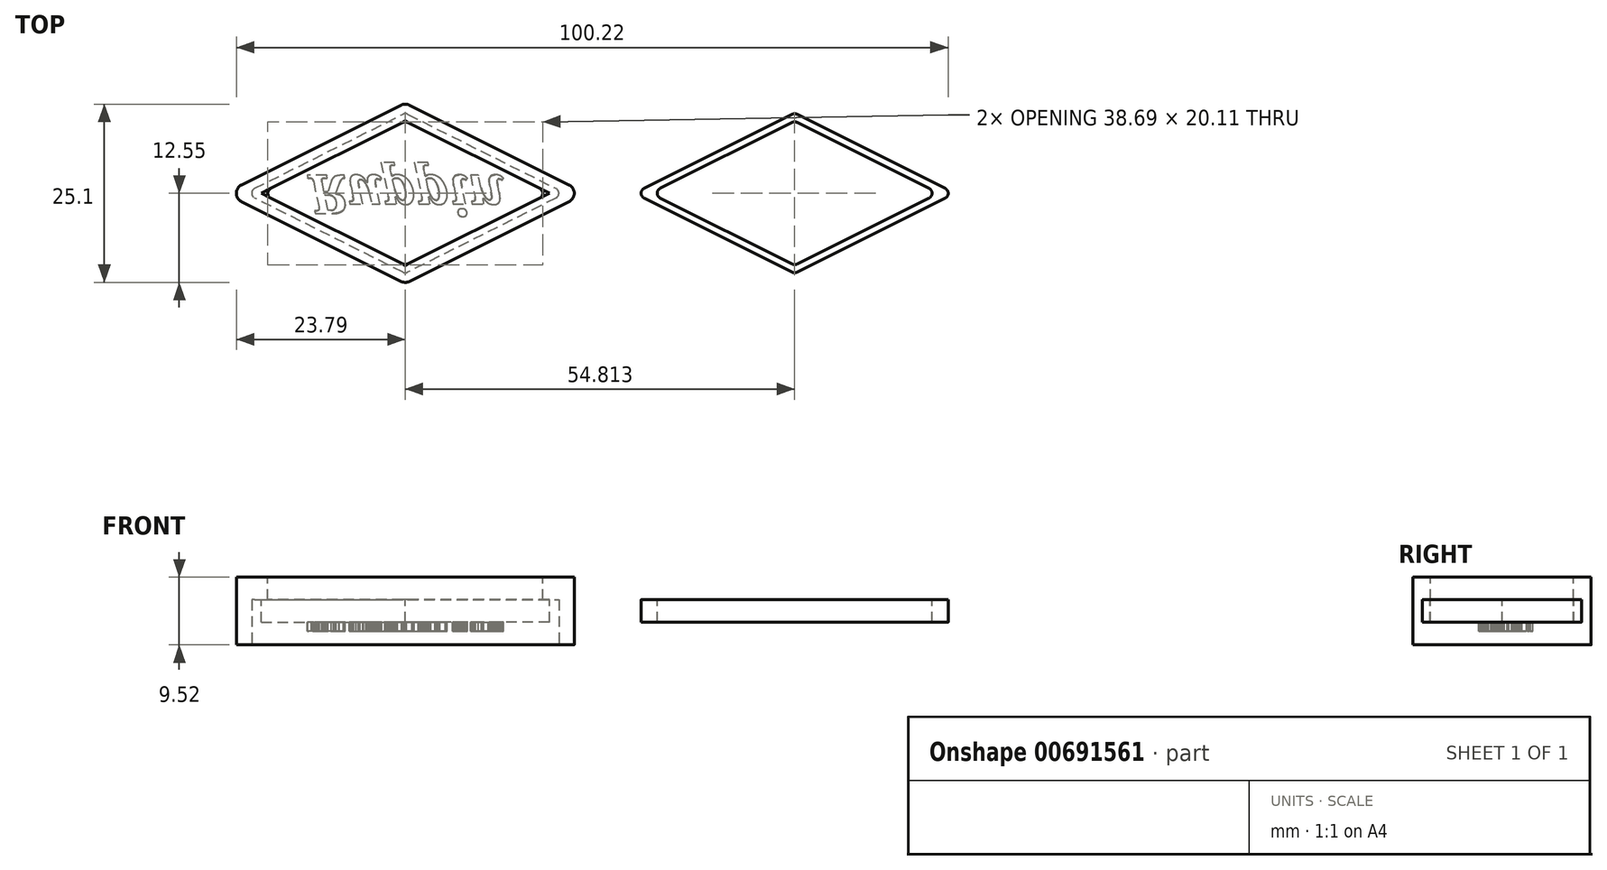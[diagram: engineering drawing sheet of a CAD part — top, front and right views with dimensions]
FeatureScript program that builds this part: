
annotation { "Feature Type Name" : "Feature", "Feature Type Description" : "" }
export const myFeature = defineFeature(function(context is Context, id is Id, definition is map)
    precondition{}
    {
        {
            var Q0;
            Q0=qCreatedBy(makeId("Top.planeOp"),FACE);
            var sketch = newSketch(context, id + "F0", { "sketchPlane" : qUnion([Q0])});
            skLineSegment(sketch, "E0", {"start": v(-23.07, 1.17) * mm, "end": v(-0.58, 12.4) * mm});
            skLineSegment(sketch, "E1", {"start": v(0.58, 12.4) * mm, "end": v(23.07, 1.17) * mm});
            skLineSegment(sketch, "E2", {"start": v(23.07, -1.17) * mm, "end": v(0.58, -12.4) * mm});
            skLineSegment(sketch, "E3", {"start": v(-0.58, -12.4) * mm, "end": v(-23.07, -1.17) * mm});
            skPoint(sketch, "E4.visualSharp", {"position": v(-25.4, 0) * mm});
            skArc(sketch, "E4.filletArc", {"start": v(-23.07, 1.17) * mm, "mid": v(-23.79, 0) * mm, "end": v(-23.07, -1.17) * mm});
            skPoint(sketch, "E5.visualSharp", {"position": v(0, 12.7) * mm});
            skArc(sketch, "E5.filletArc", {"start": v(0.58, 12.4) * mm, "mid": v(0, 12.55) * mm, "end": v(-0.58, 12.4) * mm});
            skPoint(sketch, "E6.visualSharp", {"position": v(25.4, 0) * mm});
            skArc(sketch, "E6.filletArc", {"start": v(23.07, -1.17) * mm, "mid": v(23.79, 0) * mm, "end": v(23.07, 1.17) * mm});
            skPoint(sketch, "E7.visualSharp", {"position": v(0, -12.7) * mm});
            skArc(sketch, "E7.filletArc", {"start": v(-0.58, -12.4) * mm, "mid": v(0, -12.55) * mm, "end": v(0.58, -12.4) * mm});
            skLineSegment(sketch, "E8.0", {"start": v(22.56, 0) * mm, "end": v(0, -11.28) * mm});
            skLineSegment(sketch, "E8.1", {"start": v(0, 11.28) * mm, "end": v(22.56, 0) * mm});
            skLineSegment(sketch, "E8.2", {"start": v(-22.56, 0) * mm, "end": v(0, 11.28) * mm});
            skLineSegment(sketch, "E8.3", {"start": v(0, -11.28) * mm, "end": v(-22.56, 0) * mm});
            skLineSegment(sketch, "E9.0", {"start": v(20.29, 0) * mm, "end": v(0, -10.14) * mm});
            skLineSegment(sketch, "E9.1", {"start": v(0, 10.14) * mm, "end": v(20.29, 0) * mm});
            skLineSegment(sketch, "E9.2", {"start": v(-20.29, 0) * mm, "end": v(0, 10.14) * mm});
            skLineSegment(sketch, "E9.3", {"start": v(0, -10.14) * mm, "end": v(-20.29, 0) * mm});
            skSolve(sketch);
        }
        {
            var Q0;
            Q0 = qSketchRegion(id + "F0", true);
            var Q1;
            Q1=makeQuery(id+"F0.imprint","IMPRINT",FACE,{"disambiguationData":[TD([[makeQuery(id+"F0.imprint","IMPRINT",EDGE,{"derivedFrom":sQuery(id+"F0.wireOp",EDGE,"E8.0")}),-1.0]])]});
            extrude(context, id + "F1", {"entities" : qUnion([Q0, Q1]), "depth" : 3.17 * mm, "offsetDistance" : 25.4 * mm});
        }
        {
            var Q0;
            Q0 = qSketchRegion(id + "F0", true);
            extrude(context, id + "F2", {"entities" : qUnion([Q0]), "operationType" : NewBodyOperationType.ADD, "oppositeDirection" : true, "depth" : 3.17 * mm, "offsetDistance" : 25.4 * mm});
        }
        {
            var Q0;
            Q0=makeQuery(id+"F2.opExtrude","CAP_FACE",FACE,{"disambiguationData":[OSD([sQuery(id+"F0.wireOp",EDGE,"E0"),sQuery(id+"F0.wireOp",EDGE,"E1"),sQuery(id+"F0.wireOp",EDGE,"E2"),sQuery(id+"F0.wireOp",EDGE,"E3"),sQuery(id+"F0.wireOp",EDGE,"E4.filletArc"),sQuery(id+"F0.wireOp",EDGE,"E5.filletArc"),sQuery(id+"F0.wireOp",EDGE,"E6.filletArc"),sQuery(id+"F0.wireOp",EDGE,"E7.filletArc"),sQuery(id+"F0.wireOp",EDGE,"E8.0"),sQuery(id+"F0.wireOp",EDGE,"E8.1"),sQuery(id+"F0.wireOp",EDGE,"E8.2"),sQuery(id+"F0.wireOp",EDGE,"E8.3")])],"isStart":false});
            extrude(context, id + "F3", {"entities" : qUnion([Q0]), "operationType" : NewBodyOperationType.ADD, "depth" : 3.17 * mm, "offsetDistance" : 25.4 * mm});
        }
        {
            var Q0;
            {var subQ0=sQuery(id+"F0.wireOp",EDGE,"E8.3");var subQ1=sQuery(id+"F0.wireOp",EDGE,"E8.2");Q0=makeQuery(id+"F3.boolean.opBoolean","MERGE",EDGE,{"derivedFrom":[makeQuery(id+"F2.opExtrude","SWEPT_EDGE",EDGE,{"disambiguationData":[OSD([subQ1,subQ0])]}),makeQuery(id+"F3.opExtrude","SWEPT_EDGE",EDGE,{"disambiguationData":[OSD([subQ1,subQ0])]})]});}
            var Q1;
            {var subQ0=sQuery(id+"F0.wireOp",EDGE,"E8.3");var subQ1=sQuery(id+"F0.wireOp",EDGE,"E8.0");Q1=makeQuery(id+"F3.boolean.opBoolean","MERGE",EDGE,{"derivedFrom":[makeQuery(id+"F2.opExtrude","SWEPT_EDGE",EDGE,{"disambiguationData":[OSD([subQ1,subQ0])]}),makeQuery(id+"F3.opExtrude","SWEPT_EDGE",EDGE,{"disambiguationData":[OSD([subQ1,subQ0])]})]});}
            var Q2;
            {var subQ0=sQuery(id+"F0.wireOp",EDGE,"E8.1");var subQ1=sQuery(id+"F0.wireOp",EDGE,"E8.0");Q2=makeQuery(id+"F3.boolean.opBoolean","MERGE",EDGE,{"derivedFrom":[makeQuery(id+"F2.opExtrude","SWEPT_EDGE",EDGE,{"disambiguationData":[OSD([subQ1,subQ0])]}),makeQuery(id+"F3.opExtrude","SWEPT_EDGE",EDGE,{"disambiguationData":[OSD([subQ1,subQ0])]})]});}
            var Q3;
            {var subQ0=sQuery(id+"F0.wireOp",EDGE,"E8.2");var subQ1=sQuery(id+"F0.wireOp",EDGE,"E8.1");Q3=makeQuery(id+"F3.boolean.opBoolean","MERGE",EDGE,{"derivedFrom":[makeQuery(id+"F2.opExtrude","SWEPT_EDGE",EDGE,{"disambiguationData":[OSD([subQ1,subQ0])]}),makeQuery(id+"F3.opExtrude","SWEPT_EDGE",EDGE,{"disambiguationData":[OSD([subQ1,subQ0])]})]});}
            var Q4;
            Q4=makeQuery(id+"F1.opExtrude","SWEPT_EDGE",EDGE,{"disambiguationData":[OSD([sQuery(id+"F0.wireOp",EDGE,"E9.1"),sQuery(id+"F0.wireOp",EDGE,"E9.2")])]});
            var Q5;
            Q5=makeQuery(id+"F1.opExtrude","SWEPT_EDGE",EDGE,{"disambiguationData":[OSD([sQuery(id+"F0.wireOp",EDGE,"E9.0"),sQuery(id+"F0.wireOp",EDGE,"E9.1")])]});
            var Q6;
            Q6=makeQuery(id+"F1.opExtrude","SWEPT_EDGE",EDGE,{"disambiguationData":[OSD([sQuery(id+"F0.wireOp",EDGE,"E9.0"),sQuery(id+"F0.wireOp",EDGE,"E9.3")])]});
            var Q7;
            Q7=makeQuery(id+"F1.opExtrude","SWEPT_EDGE",EDGE,{"disambiguationData":[OSD([sQuery(id+"F0.wireOp",EDGE,"E9.2"),sQuery(id+"F0.wireOp",EDGE,"E9.3")])]});
            fillet(context, id + "F4", {"entities" : qUnion([Q0, Q1, Q2, Q3, Q4, Q5, Q6, Q7]), "radius" : 0.76 * mm, "tangentPropagation" : true, "allowEdgeOverflow" : false});
        }
        {
            var Q0;
            Q0=makeQuery(id+"F1.opExtrude","CAP_FACE",FACE,{"disambiguationData":[OSD([sQuery(id+"F0.wireOp",EDGE,"E0"),sQuery(id+"F0.wireOp",EDGE,"E1"),sQuery(id+"F0.wireOp",EDGE,"E2"),sQuery(id+"F0.wireOp",EDGE,"E3"),sQuery(id+"F0.wireOp",EDGE,"E4.filletArc"),sQuery(id+"F0.wireOp",EDGE,"E5.filletArc"),sQuery(id+"F0.wireOp",EDGE,"E6.filletArc"),sQuery(id+"F0.wireOp",EDGE,"E7.filletArc"),sQuery(id+"F0.wireOp",EDGE,"E9.0"),sQuery(id+"F0.wireOp",EDGE,"E9.1"),sQuery(id+"F0.wireOp",EDGE,"E9.2"),sQuery(id+"F0.wireOp",EDGE,"E9.3")])],"isStart":true});
            var Q1;
            Q1=makeQuery(id+"F0.imprint","IMPRINT",FACE,{"disambiguationData":[TD([[makeQuery(id+"F0.imprint","IMPRINT",EDGE,{"derivedFrom":sQuery(id+"F0.wireOp",EDGE,"E9.0")}),-1.0]])]});
            extrude(context, id + "F5", {"entities" : qUnion([Q0, Q1]), "depth" : 3.17 * mm, "offsetDistance" : 25.4 * mm});
        }
        {
            var Q0;
            Q0=makeQuery(id+"F5.opExtrude","CAP_FACE",FACE,{"disambiguationData":[OSD([sQuery(id+"F0.wireOp",EDGE,"E9.0"),sQuery(id+"F0.wireOp",EDGE,"E9.1"),sQuery(id+"F0.wireOp",EDGE,"E9.2"),sQuery(id+"F0.wireOp",EDGE,"E9.3")])],"isStart":false});
            var sketch = newSketch(context, id + "F6", { "sketchPlane" : qUnion([Q0])});
            skText(sketch, "E10", { "text": "Ruppin", "fontName": "NotoSerif-BoldItalic.ttf"});
            const initialGuessF6  = {"E10": [-0.01363, -0.00254, 1, 0, 0.00544]};
            skSetInitialGuess(sketch, initialGuessF6);
            skSolve(sketch);
        }
        {
            var Q0;
            Q0 = qSketchRegion(id + "F6", true);
            extrude(context, id + "F7", {"entities" : qUnion([Q0]), "operationType" : NewBodyOperationType.ADD, "depth" : 1.27 * mm, "offsetDistance" : 25.4 * mm});
        }
        {
            var Q0;
            Q0=makeQuery(id+"F7.opExtrude","CAP_FACE",FACE,{"disambiguationData":[OSD([sQuery(id+"F6.wireOp",EDGE,"E10.sketch_text.stroke-0"),sQuery(id+"F6.wireOp",EDGE,"E10.sketch_text.stroke-1"),sQuery(id+"F6.wireOp",EDGE,"E10.sketch_text.stroke-2"),sQuery(id+"F6.wireOp",EDGE,"E10.sketch_text.stroke-3"),sQuery(id+"F6.wireOp",EDGE,"E10.sketch_text.stroke-4"),sQuery(id+"F6.wireOp",EDGE,"E10.sketch_text.stroke-5"),sQuery(id+"F6.wireOp",EDGE,"E10.sketch_text.stroke-6"),sQuery(id+"F6.wireOp",EDGE,"E10.sketch_text.stroke-7"),sQuery(id+"F6.wireOp",EDGE,"E10.sketch_text.stroke-8"),sQuery(id+"F6.wireOp",EDGE,"E10.sketch_text.stroke-9"),sQuery(id+"F6.wireOp",EDGE,"E10.sketch_text.stroke-10"),sQuery(id+"F6.wireOp",EDGE,"E10.sketch_text.stroke-11"),sQuery(id+"F6.wireOp",EDGE,"E10.sketch_text.stroke-12"),sQuery(id+"F6.wireOp",EDGE,"E10.sketch_text.stroke-13"),sQuery(id+"F6.wireOp",EDGE,"E10.sketch_text.stroke-14"),sQuery(id+"F6.wireOp",EDGE,"E10.sketch_text.stroke-15"),sQuery(id+"F6.wireOp",EDGE,"E10.sketch_text.stroke-16"),sQuery(id+"F6.wireOp",EDGE,"E10.sketch_text.stroke-17"),sQuery(id+"F6.wireOp",EDGE,"E10.sketch_text.stroke-18"),sQuery(id+"F6.wireOp",EDGE,"E10.sketch_text.stroke-19"),sQuery(id+"F6.wireOp",EDGE,"E10.sketch_text.stroke-20"),sQuery(id+"F6.wireOp",EDGE,"E10.sketch_text.stroke-21"),sQuery(id+"F6.wireOp",EDGE,"E10.sketch_text.stroke-22"),sQuery(id+"F6.wireOp",EDGE,"E10.sketch_text.stroke-23"),sQuery(id+"F6.wireOp",EDGE,"E10.sketch_text.stroke-24"),sQuery(id+"F6.wireOp",EDGE,"E10.sketch_text.stroke-25"),sQuery(id+"F6.wireOp",EDGE,"E10.sketch_text.stroke-26"),sQuery(id+"F6.wireOp",EDGE,"E10.sketch_text.stroke-27"),sQuery(id+"F6.wireOp",EDGE,"E10.sketch_text.stroke-28"),sQuery(id+"F6.wireOp",EDGE,"E10.sketch_text.stroke-29"),sQuery(id+"F6.wireOp",EDGE,"E10.sketch_text.stroke-30"),sQuery(id+"F6.wireOp",EDGE,"E10.sketch_text.stroke-31"),sQuery(id+"F6.wireOp",EDGE,"E10.sketch_text.stroke-32"),sQuery(id+"F6.wireOp",EDGE,"E10.sketch_text.stroke-33"),sQuery(id+"F6.wireOp",EDGE,"E10.sketch_text.stroke-34"),sQuery(id+"F6.wireOp",EDGE,"E10.sketch_text.stroke-35"),sQuery(id+"F6.wireOp",EDGE,"E10.sketch_text.stroke-36"),sQuery(id+"F6.wireOp",EDGE,"E10.sketch_text.stroke-37"),sQuery(id+"F6.wireOp",EDGE,"E10.sketch_text.stroke-38"),sQuery(id+"F6.wireOp",EDGE,"E10.sketch_text.stroke-39"),sQuery(id+"F6.wireOp",EDGE,"E10.sketch_text.stroke-40"),sQuery(id+"F6.wireOp",EDGE,"E10.sketch_text.stroke-41"),sQuery(id+"F6.wireOp",EDGE,"E10.sketch_text.stroke-42"),sQuery(id+"F6.wireOp",EDGE,"E10.sketch_text.stroke-43"),sQuery(id+"F6.wireOp",EDGE,"E10.sketch_text.stroke-44"),sQuery(id+"F6.wireOp",EDGE,"E10.sketch_text.stroke-45"),sQuery(id+"F6.wireOp",EDGE,"E10.sketch_text.stroke-46"),sQuery(id+"F6.wireOp",EDGE,"E10.sketch_text.stroke-47"),sQuery(id+"F6.wireOp",EDGE,"E10.sketch_text.stroke-48"),sQuery(id+"F6.wireOp",EDGE,"E10.sketch_text.stroke-49"),sQuery(id+"F6.wireOp",EDGE,"E10.sketch_text.stroke-50"),sQuery(id+"F6.wireOp",EDGE,"E10.sketch_text.stroke-51"),sQuery(id+"F6.wireOp",EDGE,"E10.sketch_text.stroke-52"),sQuery(id+"F6.wireOp",EDGE,"E10.sketch_text.stroke-53"),sQuery(id+"F6.wireOp",EDGE,"E10.sketch_text.stroke-54"),sQuery(id+"F6.wireOp",EDGE,"E10.sketch_text.stroke-55")])],"isStart":false});
            var Q1;
            Q1=makeQuery(id+"F7.opExtrude","CAP_FACE",FACE,{"disambiguationData":[OSD([sQuery(id+"F6.wireOp",EDGE,"E10.sketch_text.stroke-56"),sQuery(id+"F6.wireOp",EDGE,"E10.sketch_text.stroke-57"),sQuery(id+"F6.wireOp",EDGE,"E10.sketch_text.stroke-58"),sQuery(id+"F6.wireOp",EDGE,"E10.sketch_text.stroke-59"),sQuery(id+"F6.wireOp",EDGE,"E10.sketch_text.stroke-60"),sQuery(id+"F6.wireOp",EDGE,"E10.sketch_text.stroke-61"),sQuery(id+"F6.wireOp",EDGE,"E10.sketch_text.stroke-62"),sQuery(id+"F6.wireOp",EDGE,"E10.sketch_text.stroke-63"),sQuery(id+"F6.wireOp",EDGE,"E10.sketch_text.stroke-64"),sQuery(id+"F6.wireOp",EDGE,"E10.sketch_text.stroke-65"),sQuery(id+"F6.wireOp",EDGE,"E10.sketch_text.stroke-66"),sQuery(id+"F6.wireOp",EDGE,"E10.sketch_text.stroke-67"),sQuery(id+"F6.wireOp",EDGE,"E10.sketch_text.stroke-68"),sQuery(id+"F6.wireOp",EDGE,"E10.sketch_text.stroke-69"),sQuery(id+"F6.wireOp",EDGE,"E10.sketch_text.stroke-70"),sQuery(id+"F6.wireOp",EDGE,"E10.sketch_text.stroke-71"),sQuery(id+"F6.wireOp",EDGE,"E10.sketch_text.stroke-72"),sQuery(id+"F6.wireOp",EDGE,"E10.sketch_text.stroke-73"),sQuery(id+"F6.wireOp",EDGE,"E10.sketch_text.stroke-74"),sQuery(id+"F6.wireOp",EDGE,"E10.sketch_text.stroke-75"),sQuery(id+"F6.wireOp",EDGE,"E10.sketch_text.stroke-76"),sQuery(id+"F6.wireOp",EDGE,"E10.sketch_text.stroke-77"),sQuery(id+"F6.wireOp",EDGE,"E10.sketch_text.stroke-78"),sQuery(id+"F6.wireOp",EDGE,"E10.sketch_text.stroke-79"),sQuery(id+"F6.wireOp",EDGE,"E10.sketch_text.stroke-80"),sQuery(id+"F6.wireOp",EDGE,"E10.sketch_text.stroke-81"),sQuery(id+"F6.wireOp",EDGE,"E10.sketch_text.stroke-82"),sQuery(id+"F6.wireOp",EDGE,"E10.sketch_text.stroke-83"),sQuery(id+"F6.wireOp",EDGE,"E10.sketch_text.stroke-84"),sQuery(id+"F6.wireOp",EDGE,"E10.sketch_text.stroke-85"),sQuery(id+"F6.wireOp",EDGE,"E10.sketch_text.stroke-86"),sQuery(id+"F6.wireOp",EDGE,"E10.sketch_text.stroke-87"),sQuery(id+"F6.wireOp",EDGE,"E10.sketch_text.stroke-88"),sQuery(id+"F6.wireOp",EDGE,"E10.sketch_text.stroke-89"),sQuery(id+"F6.wireOp",EDGE,"E10.sketch_text.stroke-90"),sQuery(id+"F6.wireOp",EDGE,"E10.sketch_text.stroke-91"),sQuery(id+"F6.wireOp",EDGE,"E10.sketch_text.stroke-92"),sQuery(id+"F6.wireOp",EDGE,"E10.sketch_text.stroke-93"),sQuery(id+"F6.wireOp",EDGE,"E10.sketch_text.stroke-94"),sQuery(id+"F6.wireOp",EDGE,"E10.sketch_text.stroke-95"),sQuery(id+"F6.wireOp",EDGE,"E10.sketch_text.stroke-96"),sQuery(id+"F6.wireOp",EDGE,"E10.sketch_text.stroke-97"),sQuery(id+"F6.wireOp",EDGE,"E10.sketch_text.stroke-98"),sQuery(id+"F6.wireOp",EDGE,"E10.sketch_text.stroke-99"),sQuery(id+"F6.wireOp",EDGE,"E10.sketch_text.stroke-100"),sQuery(id+"F6.wireOp",EDGE,"E10.sketch_text.stroke-101"),sQuery(id+"F6.wireOp",EDGE,"E10.sketch_text.stroke-102"),sQuery(id+"F6.wireOp",EDGE,"E10.sketch_text.stroke-103"),sQuery(id+"F6.wireOp",EDGE,"E10.sketch_text.stroke-104"),sQuery(id+"F6.wireOp",EDGE,"E10.sketch_text.stroke-105"),sQuery(id+"F6.wireOp",EDGE,"E10.sketch_text.stroke-106"),sQuery(id+"F6.wireOp",EDGE,"E10.sketch_text.stroke-107")])],"isStart":false});
            var Q2;
            Q2=makeQuery(id+"F7.opExtrude","CAP_FACE",FACE,{"disambiguationData":[OSD([sQuery(id+"F6.wireOp",EDGE,"E10.sketch_text.stroke-174"),sQuery(id+"F6.wireOp",EDGE,"E10.sketch_text.stroke-175"),sQuery(id+"F6.wireOp",EDGE,"E10.sketch_text.stroke-176"),sQuery(id+"F6.wireOp",EDGE,"E10.sketch_text.stroke-177"),sQuery(id+"F6.wireOp",EDGE,"E10.sketch_text.stroke-178"),sQuery(id+"F6.wireOp",EDGE,"E10.sketch_text.stroke-179"),sQuery(id+"F6.wireOp",EDGE,"E10.sketch_text.stroke-180"),sQuery(id+"F6.wireOp",EDGE,"E10.sketch_text.stroke-181"),sQuery(id+"F6.wireOp",EDGE,"E10.sketch_text.stroke-182"),sQuery(id+"F6.wireOp",EDGE,"E10.sketch_text.stroke-183"),sQuery(id+"F6.wireOp",EDGE,"E10.sketch_text.stroke-184"),sQuery(id+"F6.wireOp",EDGE,"E10.sketch_text.stroke-185"),sQuery(id+"F6.wireOp",EDGE,"E10.sketch_text.stroke-186"),sQuery(id+"F6.wireOp",EDGE,"E10.sketch_text.stroke-187"),sQuery(id+"F6.wireOp",EDGE,"E10.sketch_text.stroke-188"),sQuery(id+"F6.wireOp",EDGE,"E10.sketch_text.stroke-189"),sQuery(id+"F6.wireOp",EDGE,"E10.sketch_text.stroke-190"),sQuery(id+"F6.wireOp",EDGE,"E10.sketch_text.stroke-191"),sQuery(id+"F6.wireOp",EDGE,"E10.sketch_text.stroke-192"),sQuery(id+"F6.wireOp",EDGE,"E10.sketch_text.stroke-193"),sQuery(id+"F6.wireOp",EDGE,"E10.sketch_text.stroke-194"),sQuery(id+"F6.wireOp",EDGE,"E10.sketch_text.stroke-195"),sQuery(id+"F6.wireOp",EDGE,"E10.sketch_text.stroke-196"),sQuery(id+"F6.wireOp",EDGE,"E10.sketch_text.stroke-197"),sQuery(id+"F6.wireOp",EDGE,"E10.sketch_text.stroke-198"),sQuery(id+"F6.wireOp",EDGE,"E10.sketch_text.stroke-199"),sQuery(id+"F6.wireOp",EDGE,"E10.sketch_text.stroke-200"),sQuery(id+"F6.wireOp",EDGE,"E10.sketch_text.stroke-201"),sQuery(id+"F6.wireOp",EDGE,"E10.sketch_text.stroke-202"),sQuery(id+"F6.wireOp",EDGE,"E10.sketch_text.stroke-203"),sQuery(id+"F6.wireOp",EDGE,"E10.sketch_text.stroke-204"),sQuery(id+"F6.wireOp",EDGE,"E10.sketch_text.stroke-205"),sQuery(id+"F6.wireOp",EDGE,"E10.sketch_text.stroke-206"),sQuery(id+"F6.wireOp",EDGE,"E10.sketch_text.stroke-207"),sQuery(id+"F6.wireOp",EDGE,"E10.sketch_text.stroke-208"),sQuery(id+"F6.wireOp",EDGE,"E10.sketch_text.stroke-209"),sQuery(id+"F6.wireOp",EDGE,"E10.sketch_text.stroke-210"),sQuery(id+"F6.wireOp",EDGE,"E10.sketch_text.stroke-211"),sQuery(id+"F6.wireOp",EDGE,"E10.sketch_text.stroke-212"),sQuery(id+"F6.wireOp",EDGE,"E10.sketch_text.stroke-213"),sQuery(id+"F6.wireOp",EDGE,"E10.sketch_text.stroke-214"),sQuery(id+"F6.wireOp",EDGE,"E10.sketch_text.stroke-215"),sQuery(id+"F6.wireOp",EDGE,"E10.sketch_text.stroke-216"),sQuery(id+"F6.wireOp",EDGE,"E10.sketch_text.stroke-217"),sQuery(id+"F6.wireOp",EDGE,"E10.sketch_text.stroke-218"),sQuery(id+"F6.wireOp",EDGE,"E10.sketch_text.stroke-219"),sQuery(id+"F6.wireOp",EDGE,"E10.sketch_text.stroke-220"),sQuery(id+"F6.wireOp",EDGE,"E10.sketch_text.stroke-221"),sQuery(id+"F6.wireOp",EDGE,"E10.sketch_text.stroke-222"),sQuery(id+"F6.wireOp",EDGE,"E10.sketch_text.stroke-223"),sQuery(id+"F6.wireOp",EDGE,"E10.sketch_text.stroke-224"),sQuery(id+"F6.wireOp",EDGE,"E10.sketch_text.stroke-225"),sQuery(id+"F6.wireOp",EDGE,"E10.sketch_text.stroke-226"),sQuery(id+"F6.wireOp",EDGE,"E10.sketch_text.stroke-227"),sQuery(id+"F6.wireOp",EDGE,"E10.sketch_text.stroke-228"),sQuery(id+"F6.wireOp",EDGE,"E10.sketch_text.stroke-229"),sQuery(id+"F6.wireOp",EDGE,"E10.sketch_text.stroke-230"),sQuery(id+"F6.wireOp",EDGE,"E10.sketch_text.stroke-231"),sQuery(id+"F6.wireOp",EDGE,"E10.sketch_text.stroke-232"),sQuery(id+"F6.wireOp",EDGE,"E10.sketch_text.stroke-233"),sQuery(id+"F6.wireOp",EDGE,"E10.sketch_text.stroke-234"),sQuery(id+"F6.wireOp",EDGE,"E10.sketch_text.stroke-235"),sQuery(id+"F6.wireOp",EDGE,"E10.sketch_text.stroke-236"),sQuery(id+"F6.wireOp",EDGE,"E10.sketch_text.stroke-237"),sQuery(id+"F6.wireOp",EDGE,"E10.sketch_text.stroke-238"),sQuery(id+"F6.wireOp",EDGE,"E10.sketch_text.stroke-239")])],"isStart":false});
            var Q3;
            Q3=makeQuery(id+"F7.opExtrude","CAP_FACE",FACE,{"disambiguationData":[OSD([sQuery(id+"F6.wireOp",EDGE,"E10.sketch_text.stroke-108"),sQuery(id+"F6.wireOp",EDGE,"E10.sketch_text.stroke-109"),sQuery(id+"F6.wireOp",EDGE,"E10.sketch_text.stroke-110"),sQuery(id+"F6.wireOp",EDGE,"E10.sketch_text.stroke-111"),sQuery(id+"F6.wireOp",EDGE,"E10.sketch_text.stroke-112"),sQuery(id+"F6.wireOp",EDGE,"E10.sketch_text.stroke-113"),sQuery(id+"F6.wireOp",EDGE,"E10.sketch_text.stroke-114"),sQuery(id+"F6.wireOp",EDGE,"E10.sketch_text.stroke-115"),sQuery(id+"F6.wireOp",EDGE,"E10.sketch_text.stroke-116"),sQuery(id+"F6.wireOp",EDGE,"E10.sketch_text.stroke-117"),sQuery(id+"F6.wireOp",EDGE,"E10.sketch_text.stroke-118"),sQuery(id+"F6.wireOp",EDGE,"E10.sketch_text.stroke-119"),sQuery(id+"F6.wireOp",EDGE,"E10.sketch_text.stroke-120"),sQuery(id+"F6.wireOp",EDGE,"E10.sketch_text.stroke-121"),sQuery(id+"F6.wireOp",EDGE,"E10.sketch_text.stroke-122"),sQuery(id+"F6.wireOp",EDGE,"E10.sketch_text.stroke-123"),sQuery(id+"F6.wireOp",EDGE,"E10.sketch_text.stroke-124"),sQuery(id+"F6.wireOp",EDGE,"E10.sketch_text.stroke-125"),sQuery(id+"F6.wireOp",EDGE,"E10.sketch_text.stroke-126"),sQuery(id+"F6.wireOp",EDGE,"E10.sketch_text.stroke-127"),sQuery(id+"F6.wireOp",EDGE,"E10.sketch_text.stroke-128"),sQuery(id+"F6.wireOp",EDGE,"E10.sketch_text.stroke-129"),sQuery(id+"F6.wireOp",EDGE,"E10.sketch_text.stroke-130"),sQuery(id+"F6.wireOp",EDGE,"E10.sketch_text.stroke-131"),sQuery(id+"F6.wireOp",EDGE,"E10.sketch_text.stroke-132"),sQuery(id+"F6.wireOp",EDGE,"E10.sketch_text.stroke-133"),sQuery(id+"F6.wireOp",EDGE,"E10.sketch_text.stroke-134"),sQuery(id+"F6.wireOp",EDGE,"E10.sketch_text.stroke-135"),sQuery(id+"F6.wireOp",EDGE,"E10.sketch_text.stroke-136"),sQuery(id+"F6.wireOp",EDGE,"E10.sketch_text.stroke-137"),sQuery(id+"F6.wireOp",EDGE,"E10.sketch_text.stroke-138"),sQuery(id+"F6.wireOp",EDGE,"E10.sketch_text.stroke-139"),sQuery(id+"F6.wireOp",EDGE,"E10.sketch_text.stroke-140"),sQuery(id+"F6.wireOp",EDGE,"E10.sketch_text.stroke-141"),sQuery(id+"F6.wireOp",EDGE,"E10.sketch_text.stroke-142"),sQuery(id+"F6.wireOp",EDGE,"E10.sketch_text.stroke-143"),sQuery(id+"F6.wireOp",EDGE,"E10.sketch_text.stroke-144"),sQuery(id+"F6.wireOp",EDGE,"E10.sketch_text.stroke-145"),sQuery(id+"F6.wireOp",EDGE,"E10.sketch_text.stroke-146"),sQuery(id+"F6.wireOp",EDGE,"E10.sketch_text.stroke-147"),sQuery(id+"F6.wireOp",EDGE,"E10.sketch_text.stroke-148"),sQuery(id+"F6.wireOp",EDGE,"E10.sketch_text.stroke-149"),sQuery(id+"F6.wireOp",EDGE,"E10.sketch_text.stroke-150"),sQuery(id+"F6.wireOp",EDGE,"E10.sketch_text.stroke-151"),sQuery(id+"F6.wireOp",EDGE,"E10.sketch_text.stroke-152"),sQuery(id+"F6.wireOp",EDGE,"E10.sketch_text.stroke-153"),sQuery(id+"F6.wireOp",EDGE,"E10.sketch_text.stroke-154"),sQuery(id+"F6.wireOp",EDGE,"E10.sketch_text.stroke-155"),sQuery(id+"F6.wireOp",EDGE,"E10.sketch_text.stroke-156"),sQuery(id+"F6.wireOp",EDGE,"E10.sketch_text.stroke-157"),sQuery(id+"F6.wireOp",EDGE,"E10.sketch_text.stroke-158"),sQuery(id+"F6.wireOp",EDGE,"E10.sketch_text.stroke-159"),sQuery(id+"F6.wireOp",EDGE,"E10.sketch_text.stroke-160"),sQuery(id+"F6.wireOp",EDGE,"E10.sketch_text.stroke-161"),sQuery(id+"F6.wireOp",EDGE,"E10.sketch_text.stroke-162"),sQuery(id+"F6.wireOp",EDGE,"E10.sketch_text.stroke-163"),sQuery(id+"F6.wireOp",EDGE,"E10.sketch_text.stroke-164"),sQuery(id+"F6.wireOp",EDGE,"E10.sketch_text.stroke-165"),sQuery(id+"F6.wireOp",EDGE,"E10.sketch_text.stroke-166"),sQuery(id+"F6.wireOp",EDGE,"E10.sketch_text.stroke-167"),sQuery(id+"F6.wireOp",EDGE,"E10.sketch_text.stroke-168"),sQuery(id+"F6.wireOp",EDGE,"E10.sketch_text.stroke-169"),sQuery(id+"F6.wireOp",EDGE,"E10.sketch_text.stroke-170"),sQuery(id+"F6.wireOp",EDGE,"E10.sketch_text.stroke-171"),sQuery(id+"F6.wireOp",EDGE,"E10.sketch_text.stroke-172"),sQuery(id+"F6.wireOp",EDGE,"E10.sketch_text.stroke-173")])],"isStart":false});
            var Q4;
            Q4=makeQuery(id+"F7.opExtrude","CAP_FACE",FACE,{"disambiguationData":[OSD([sQuery(id+"F6.wireOp",EDGE,"E10.sketch_text.stroke-240"),sQuery(id+"F6.wireOp",EDGE,"E10.sketch_text.stroke-241"),sQuery(id+"F6.wireOp",EDGE,"E10.sketch_text.stroke-242"),sQuery(id+"F6.wireOp",EDGE,"E10.sketch_text.stroke-243"),sQuery(id+"F6.wireOp",EDGE,"E10.sketch_text.stroke-244"),sQuery(id+"F6.wireOp",EDGE,"E10.sketch_text.stroke-245"),sQuery(id+"F6.wireOp",EDGE,"E10.sketch_text.stroke-246"),sQuery(id+"F6.wireOp",EDGE,"E10.sketch_text.stroke-247"),sQuery(id+"F6.wireOp",EDGE,"E10.sketch_text.stroke-248"),sQuery(id+"F6.wireOp",EDGE,"E10.sketch_text.stroke-249"),sQuery(id+"F6.wireOp",EDGE,"E10.sketch_text.stroke-250"),sQuery(id+"F6.wireOp",EDGE,"E10.sketch_text.stroke-251"),sQuery(id+"F6.wireOp",EDGE,"E10.sketch_text.stroke-252"),sQuery(id+"F6.wireOp",EDGE,"E10.sketch_text.stroke-253"),sQuery(id+"F6.wireOp",EDGE,"E10.sketch_text.stroke-254"),sQuery(id+"F6.wireOp",EDGE,"E10.sketch_text.stroke-255"),sQuery(id+"F6.wireOp",EDGE,"E10.sketch_text.stroke-256"),sQuery(id+"F6.wireOp",EDGE,"E10.sketch_text.stroke-257"),sQuery(id+"F6.wireOp",EDGE,"E10.sketch_text.stroke-258"),sQuery(id+"F6.wireOp",EDGE,"E10.sketch_text.stroke-259"),sQuery(id+"F6.wireOp",EDGE,"E10.sketch_text.stroke-260"),sQuery(id+"F6.wireOp",EDGE,"E10.sketch_text.stroke-261"),sQuery(id+"F6.wireOp",EDGE,"E10.sketch_text.stroke-262"),sQuery(id+"F6.wireOp",EDGE,"E10.sketch_text.stroke-263"),sQuery(id+"F6.wireOp",EDGE,"E10.sketch_text.stroke-264"),sQuery(id+"F6.wireOp",EDGE,"E10.sketch_text.stroke-265"),sQuery(id+"F6.wireOp",EDGE,"E10.sketch_text.stroke-266"),sQuery(id+"F6.wireOp",EDGE,"E10.sketch_text.stroke-267")])],"isStart":false});
            var Q5;
            Q5=makeQuery(id+"F7.opExtrude","CAP_FACE",FACE,{"disambiguationData":[OSD([sQuery(id+"F6.wireOp",EDGE,"E10.sketch_text.stroke-284"),sQuery(id+"F6.wireOp",EDGE,"E10.sketch_text.stroke-285"),sQuery(id+"F6.wireOp",EDGE,"E10.sketch_text.stroke-286"),sQuery(id+"F6.wireOp",EDGE,"E10.sketch_text.stroke-287"),sQuery(id+"F6.wireOp",EDGE,"E10.sketch_text.stroke-288"),sQuery(id+"F6.wireOp",EDGE,"E10.sketch_text.stroke-289"),sQuery(id+"F6.wireOp",EDGE,"E10.sketch_text.stroke-290"),sQuery(id+"F6.wireOp",EDGE,"E10.sketch_text.stroke-291"),sQuery(id+"F6.wireOp",EDGE,"E10.sketch_text.stroke-292"),sQuery(id+"F6.wireOp",EDGE,"E10.sketch_text.stroke-293"),sQuery(id+"F6.wireOp",EDGE,"E10.sketch_text.stroke-294"),sQuery(id+"F6.wireOp",EDGE,"E10.sketch_text.stroke-295"),sQuery(id+"F6.wireOp",EDGE,"E10.sketch_text.stroke-296"),sQuery(id+"F6.wireOp",EDGE,"E10.sketch_text.stroke-297"),sQuery(id+"F6.wireOp",EDGE,"E10.sketch_text.stroke-298"),sQuery(id+"F6.wireOp",EDGE,"E10.sketch_text.stroke-299"),sQuery(id+"F6.wireOp",EDGE,"E10.sketch_text.stroke-300"),sQuery(id+"F6.wireOp",EDGE,"E10.sketch_text.stroke-301"),sQuery(id+"F6.wireOp",EDGE,"E10.sketch_text.stroke-302"),sQuery(id+"F6.wireOp",EDGE,"E10.sketch_text.stroke-303"),sQuery(id+"F6.wireOp",EDGE,"E10.sketch_text.stroke-304"),sQuery(id+"F6.wireOp",EDGE,"E10.sketch_text.stroke-305"),sQuery(id+"F6.wireOp",EDGE,"E10.sketch_text.stroke-306"),sQuery(id+"F6.wireOp",EDGE,"E10.sketch_text.stroke-307"),sQuery(id+"F6.wireOp",EDGE,"E10.sketch_text.stroke-308"),sQuery(id+"F6.wireOp",EDGE,"E10.sketch_text.stroke-309"),sQuery(id+"F6.wireOp",EDGE,"E10.sketch_text.stroke-310"),sQuery(id+"F6.wireOp",EDGE,"E10.sketch_text.stroke-311"),sQuery(id+"F6.wireOp",EDGE,"E10.sketch_text.stroke-312"),sQuery(id+"F6.wireOp",EDGE,"E10.sketch_text.stroke-313"),sQuery(id+"F6.wireOp",EDGE,"E10.sketch_text.stroke-314"),sQuery(id+"F6.wireOp",EDGE,"E10.sketch_text.stroke-315"),sQuery(id+"F6.wireOp",EDGE,"E10.sketch_text.stroke-316"),sQuery(id+"F6.wireOp",EDGE,"E10.sketch_text.stroke-317"),sQuery(id+"F6.wireOp",EDGE,"E10.sketch_text.stroke-318"),sQuery(id+"F6.wireOp",EDGE,"E10.sketch_text.stroke-319"),sQuery(id+"F6.wireOp",EDGE,"E10.sketch_text.stroke-320"),sQuery(id+"F6.wireOp",EDGE,"E10.sketch_text.stroke-321"),sQuery(id+"F6.wireOp",EDGE,"E10.sketch_text.stroke-322"),sQuery(id+"F6.wireOp",EDGE,"E10.sketch_text.stroke-323"),sQuery(id+"F6.wireOp",EDGE,"E10.sketch_text.stroke-324"),sQuery(id+"F6.wireOp",EDGE,"E10.sketch_text.stroke-325"),sQuery(id+"F6.wireOp",EDGE,"E10.sketch_text.stroke-326"),sQuery(id+"F6.wireOp",EDGE,"E10.sketch_text.stroke-327"),sQuery(id+"F6.wireOp",EDGE,"E10.sketch_text.stroke-328"),sQuery(id+"F6.wireOp",EDGE,"E10.sketch_text.stroke-329"),sQuery(id+"F6.wireOp",EDGE,"E10.sketch_text.stroke-330"),sQuery(id+"F6.wireOp",EDGE,"E10.sketch_text.stroke-331"),sQuery(id+"F6.wireOp",EDGE,"E10.sketch_text.stroke-332"),sQuery(id+"F6.wireOp",EDGE,"E10.sketch_text.stroke-333"),sQuery(id+"F6.wireOp",EDGE,"E10.sketch_text.stroke-334"),sQuery(id+"F6.wireOp",EDGE,"E10.sketch_text.stroke-335"),sQuery(id+"F6.wireOp",EDGE,"E10.sketch_text.stroke-336"),sQuery(id+"F6.wireOp",EDGE,"E10.sketch_text.stroke-337"),sQuery(id+"F6.wireOp",EDGE,"E10.sketch_text.stroke-338"),sQuery(id+"F6.wireOp",EDGE,"E10.sketch_text.stroke-339"),sQuery(id+"F6.wireOp",EDGE,"E10.sketch_text.stroke-340"),sQuery(id+"F6.wireOp",EDGE,"E10.sketch_text.stroke-341")])],"isStart":false});
            var Q6;
            Q6=makeQuery(id+"F7.opExtrude","CAP_FACE",FACE,{"disambiguationData":[OSD([sQuery(id+"F6.wireOp",EDGE,"E10.sketch_text.stroke-268"),sQuery(id+"F6.wireOp",EDGE,"E10.sketch_text.stroke-269"),sQuery(id+"F6.wireOp",EDGE,"E10.sketch_text.stroke-270"),sQuery(id+"F6.wireOp",EDGE,"E10.sketch_text.stroke-271"),sQuery(id+"F6.wireOp",EDGE,"E10.sketch_text.stroke-272"),sQuery(id+"F6.wireOp",EDGE,"E10.sketch_text.stroke-273"),sQuery(id+"F6.wireOp",EDGE,"E10.sketch_text.stroke-274"),sQuery(id+"F6.wireOp",EDGE,"E10.sketch_text.stroke-275"),sQuery(id+"F6.wireOp",EDGE,"E10.sketch_text.stroke-276"),sQuery(id+"F6.wireOp",EDGE,"E10.sketch_text.stroke-277"),sQuery(id+"F6.wireOp",EDGE,"E10.sketch_text.stroke-278"),sQuery(id+"F6.wireOp",EDGE,"E10.sketch_text.stroke-279"),sQuery(id+"F6.wireOp",EDGE,"E10.sketch_text.stroke-280"),sQuery(id+"F6.wireOp",EDGE,"E10.sketch_text.stroke-281"),sQuery(id+"F6.wireOp",EDGE,"E10.sketch_text.stroke-282"),sQuery(id+"F6.wireOp",EDGE,"E10.sketch_text.stroke-283")])],"isStart":false});
            fillet(context, id + "F8", {"entities" : qUnion([Q0, Q1, Q2, Q3, Q4, Q5, Q6]), "radius" : 0.03 * mm, "tangentPropagation" : true, "allowEdgeOverflow" : false});
        }
        {
            var Q0;
            Q0=makeQuery(id+"F5.opExtrude","SWEPT_BODY",BODY,{"disambiguationData":[OSD([sQuery(id+"F0.wireOp",EDGE,"E0"),sQuery(id+"F0.wireOp",EDGE,"E1"),sQuery(id+"F0.wireOp",EDGE,"E2"),sQuery(id+"F0.wireOp",EDGE,"E3"),sQuery(id+"F0.wireOp",EDGE,"E4.filletArc"),sQuery(id+"F0.wireOp",EDGE,"E5.filletArc"),sQuery(id+"F0.wireOp",EDGE,"E6.filletArc"),sQuery(id+"F0.wireOp",EDGE,"E7.filletArc"),sQuery(id+"F0.wireOp",EDGE,"E9.0"),sQuery(id+"F0.wireOp",EDGE,"E9.1"),sQuery(id+"F0.wireOp",EDGE,"E9.2"),sQuery(id+"F0.wireOp",EDGE,"E9.3")])]});
            transform(context, id + "F9", {"entities" : qUnion([Q0]), "transformType" : TransformType.TRANSLATION_3D, "dx" : 54.81 * mm, "dy" : 0 * mm, "dz" : 0 * mm, "makeCopy" : false});
        }
    });
